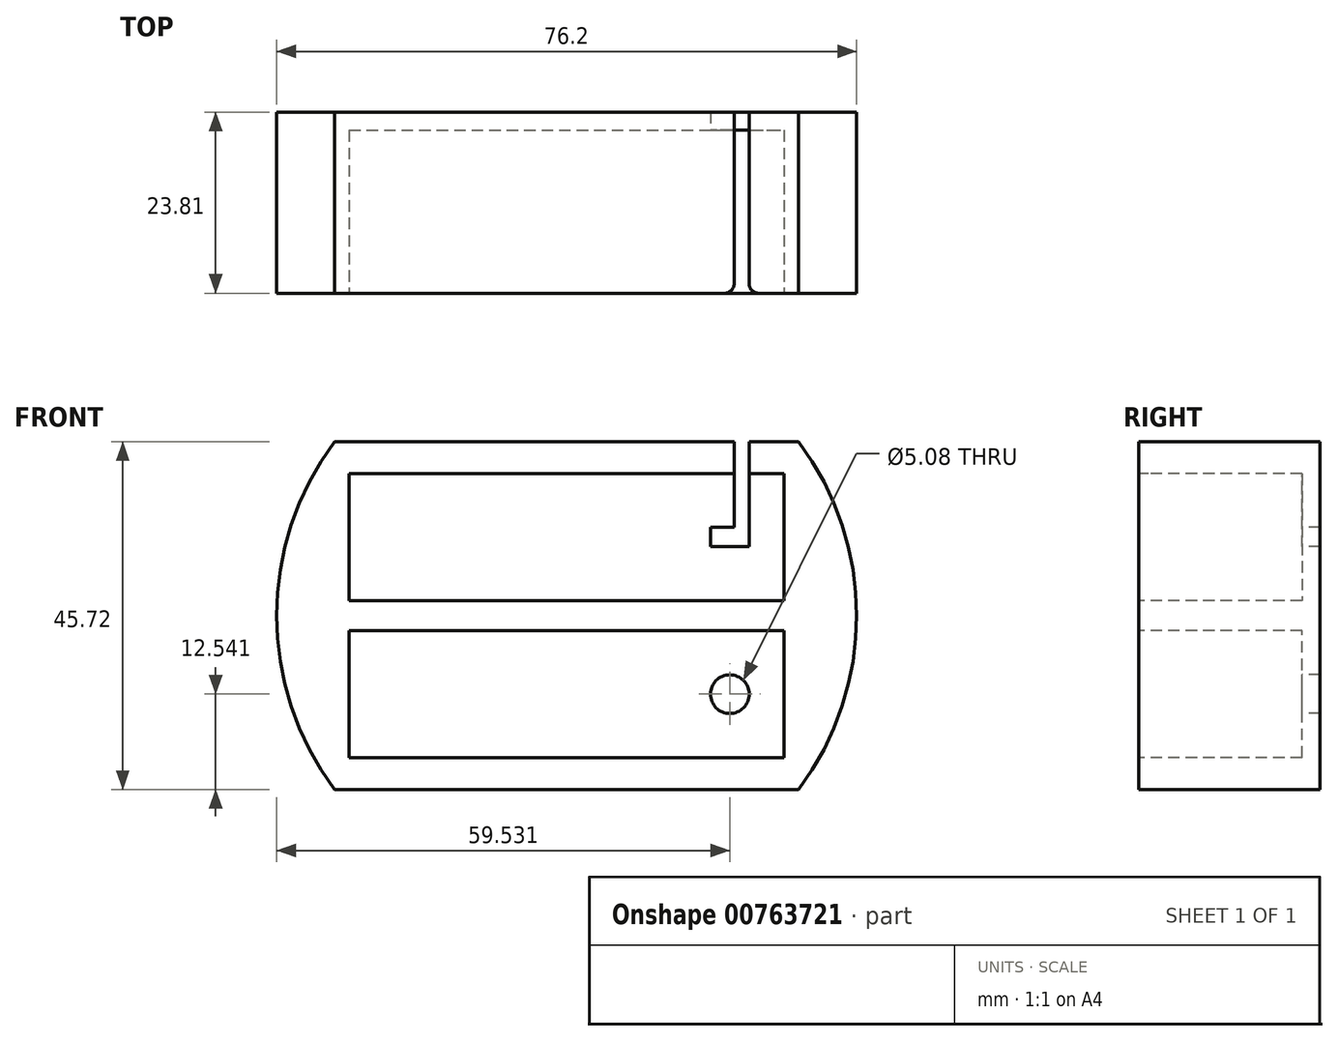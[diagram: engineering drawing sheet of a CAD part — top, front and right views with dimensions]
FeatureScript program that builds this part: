
annotation { "Feature Type Name" : "Feature", "Feature Type Description" : "" }
export const myFeature = defineFeature(function(context is Context, id is Id, definition is map)
    precondition{}
    {
        {
            var Q0;
            Q0=qCreatedBy(makeId("Front.planeOp"),FACE);
            var sketch = newSketch(context, id + "F0", { "sketchPlane" : qUnion([Q0])});
            skCircle(sketch, "E0", {"center": v(0, 0) * mm, "radius": 38.1 * mm});
            skSolve(sketch);
        }
        {
            var Q0;
            Q0=makeQuery(id+"F0.imprint","IMPRINT",FACE,{"disambiguationData":[TD([[makeQuery(id+"F0.imprint","IMPRINT",EDGE,{"derivedFrom":sQuery(id+"F0.wireOp",EDGE,"E0")}),1.0]])]});
            extrude(context, id + "F1", {"entities" : qUnion([Q0]), "depth" : 23.8 * mm, "offsetDistance" : 25.4 * mm});
        }
        {
            var Q0;
            Q0=makeQuery(id+"F1.opExtrude","CAP_FACE",FACE,{"disambiguationData":[OSD([sQuery(id+"F0.wireOp",EDGE,"E0")])],"isStart":false});
            var sketch = newSketch(context, id + "F2", { "sketchPlane" : qUnion([Q0])});
            skLineSegment(sketch, "E1.bottom", {"start": v(-28.57, 18.65) * mm, "end": v(28.58, 18.65) * mm});
            skLineSegment(sketch, "E1.top", {"start": v(-28.57, 1.98) * mm, "end": v(28.58, 1.98) * mm});
            skLineSegment(sketch, "E1.left", {"start": v(-28.57, 18.65) * mm, "end": v(-28.57, 1.98) * mm});
            skLineSegment(sketch, "E1.right", {"start": v(28.58, 18.65) * mm, "end": v(28.58, 1.98) * mm});
            skLineSegment(sketch, "E2.MirrorCS", {"start": v(-28.57, -18.65) * mm, "end": v(-28.57, -1.98) * mm});
            skLineSegment(sketch, "E3.MirrorCS", {"start": v(-28.57, -1.98) * mm, "end": v(28.58, -1.98) * mm});
            skLineSegment(sketch, "E4.MirrorCS", {"start": v(-28.57, -18.65) * mm, "end": v(28.58, -18.65) * mm});
            skLineSegment(sketch, "E5.MirrorCS", {"start": v(28.58, -18.65) * mm, "end": v(28.58, -1.98) * mm});
            skSolve(sketch);
        }
        {
            var Q0;
            Q0 = qSketchRegion(id + "F2", true);
            extrude(context, id + "F3", {"entities" : qUnion([Q0]), "operationType" : NewBodyOperationType.REMOVE, "oppositeDirection" : true, "depth" : 21.43 * mm, "offsetDistance" : 25.4 * mm});
        }
        {
            var Q0;
            Q0=makeQuery(id+"F1.opExtrude","CAP_FACE",FACE,{"disambiguationData":[OSD([sQuery(id+"F0.wireOp",EDGE,"E0")])],"isStart":false});
            var sketch = newSketch(context, id + "F4", { "sketchPlane" : qUnion([Q0])});
            skCircle(sketch, "E6", {"center": v(0, 0) * mm, "radius": 38.1 * mm});
            skLineSegment(sketch, "E7", {"start": v(-30.48, 22.86) * mm, "end": v(30.48, 22.86) * mm});
            skLineSegment(sketch, "E8", {"start": v(-30.48, -22.86) * mm, "end": v(30.48, -22.86) * mm});
            skSolve(sketch);
        }
        {
            var Q0;
            {var subQ0=sQuery(id+"F4.wireOp",EDGE,"E7");Q0=makeQuery(id+"F4.imprint","IMPRINT",FACE,{"disambiguationData":[TD([[makeQuery(id+"F4.imprint","IMPRINT",EDGE,{"derivedFrom":subQ0}),1.0]])]});}
            var Q1;
            {var subQ0=sQuery(id+"F4.wireOp",EDGE,"E8");Q1=makeQuery(id+"F4.imprint","IMPRINT",FACE,{"disambiguationData":[TD([[makeQuery(id+"F4.imprint","IMPRINT",EDGE,{"derivedFrom":subQ0}),-1.0]])]});}
            extrude(context, id + "F5", {"entities" : qUnion([Q0, Q1]), "operationType" : NewBodyOperationType.REMOVE, "oppositeDirection" : true, "depth" : 25.4 * mm, "offsetDistance" : 25.4 * mm});
        }
        {
            var Q0;
            Q0=makeQuery(id+"F3.boolean.opBoolean","COPY",FACE,{"derivedFrom":makeQuery(id+"F3.opExtrude","CAP_FACE",FACE,{"disambiguationData":[OSD([sQuery(id+"F2.wireOp",EDGE,"E2.MirrorCS"),sQuery(id+"F2.wireOp",EDGE,"E3.MirrorCS"),sQuery(id+"F2.wireOp",EDGE,"E4.MirrorCS"),sQuery(id+"F2.wireOp",EDGE,"E5.MirrorCS")])],"isStart":false})});
            var sketch = newSketch(context, id + "F6", { "sketchPlane" : qUnion([Q0])});
            skCircle(sketch, "E9", {"center": v(21.43, -10.32) * mm, "radius": 2.54 * mm});
            skPoint(sketch, "E9.centerSnap0", {"position": v(28.58, -10.32) * mm});
            skLineSegment(sketch, "E10.bottom", {"start": v(23.97, 9.05) * mm, "end": v(18.9, 9.05) * mm});
            skLineSegment(sketch, "E10.top", {"start": v(23.97, 11.59) * mm, "end": v(18.9, 11.59) * mm});
            skLineSegment(sketch, "E10.left", {"start": v(23.97, 9.05) * mm, "end": v(23.97, 11.59) * mm});
            skLineSegment(sketch, "E10.right", {"start": v(18.9, 9.05) * mm, "end": v(18.9, 11.59) * mm});
            skLineSegment(sketch, "E11", {"start": v(18.9, 10.32) * mm, "end": v(23.97, 10.32) * mm, "construction": true});
            skLineSegment(sketch, "E12", {"start": v(21.43, 11.94) * mm, "end": v(21.43, 9.05) * mm, "construction": true});
            skPoint(sketch, "E12.startSnap0", {"position": v(21.43, 11.59) * mm});
            skLineSegment(sketch, "E13.bottom", {"start": v(23.97, 11.59) * mm, "end": v(22, 11.59) * mm});
            skLineSegment(sketch, "E13.top", {"start": v(23.97, 23.59) * mm, "end": v(22, 23.59) * mm});
            skLineSegment(sketch, "E13.left", {"start": v(23.97, 11.59) * mm, "end": v(23.97, 23.59) * mm});
            skLineSegment(sketch, "E13.right", {"start": v(22, 11.59) * mm, "end": v(22, 23.59) * mm});
            skSolve(sketch);
        }
        {
            var Q0;
            Q0 = qSketchRegion(id + "F6", true);
            extrude(context, id + "F7", {"entities" : qUnion([Q0]), "operationType" : NewBodyOperationType.REMOVE, "endBound" : BoundingType.SYMMETRIC, "oppositeDirection" : true, "depth" : 50.8 * mm, "offsetDistance" : 25.4 * mm});
        }
        {
            var Q0;
            Q0=makeQuery(id+"F7.boolean.opBoolean","INTERSECT",EDGE,{"derivedFrom":[makeQuery(id+"F1.opExtrude","CAP_FACE",FACE,{"disambiguationData":[OSD([sQuery(id+"F0.wireOp",EDGE,"E0")])],"isStart":false}),makeQuery(id+"F7.opExtrude","SWEPT_FACE",FACE,{"disambiguationData":[OSD([sQuery(id+"F6.wireOp",EDGE,"E10.left"),sQuery(id+"F6.wireOp",EDGE,"E13.left")])]})]});
            var Q1;
            Q1=makeQuery(id+"F7.boolean.opBoolean","INTERSECT",EDGE,{"derivedFrom":[makeQuery(id+"F1.opExtrude","CAP_FACE",FACE,{"disambiguationData":[OSD([sQuery(id+"F0.wireOp",EDGE,"E0")])],"isStart":false}),makeQuery(id+"F7.opExtrude","SWEPT_FACE",FACE,{"disambiguationData":[OSD([sQuery(id+"F6.wireOp",EDGE,"E13.right")])]})]});
            fillet(context, id + "F8", {"entities" : qUnion([Q0, Q1]), "radius" : 1.27 * mm, "tangentPropagation" : true, "allowEdgeOverflow" : false});
        }
    });
